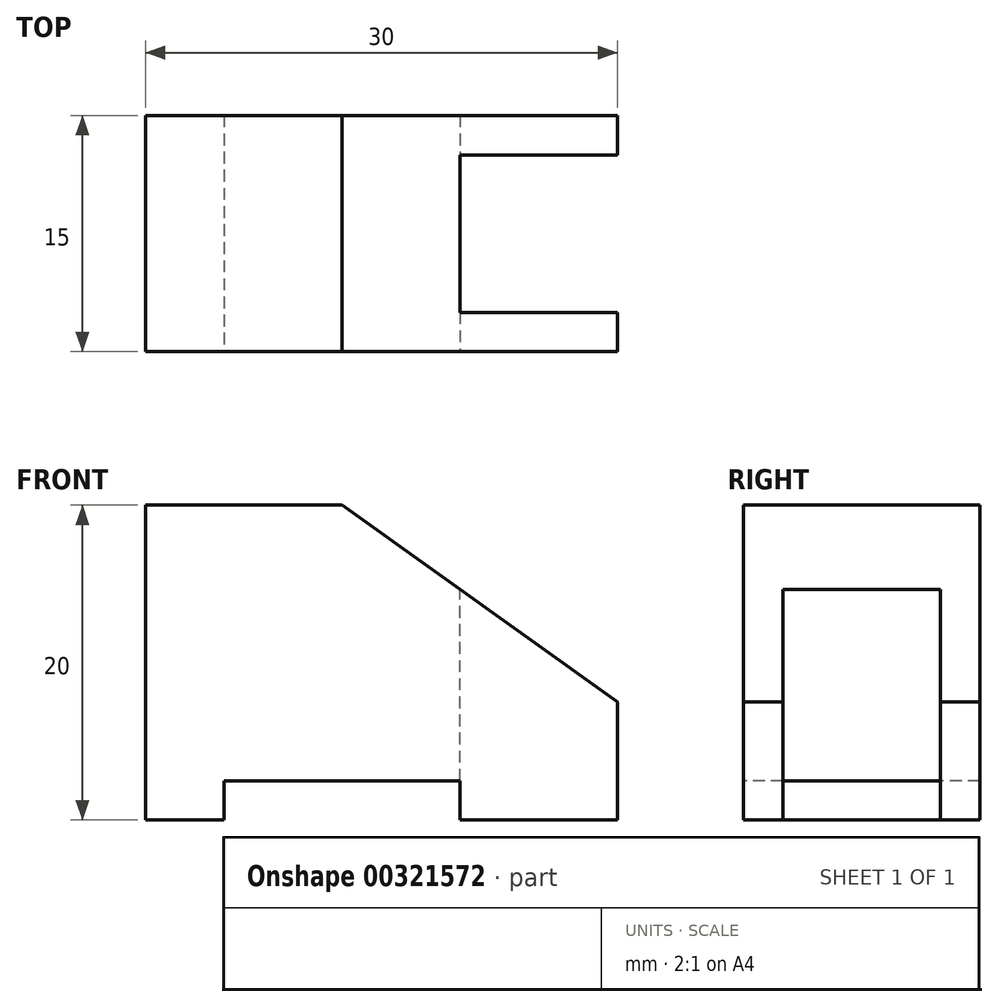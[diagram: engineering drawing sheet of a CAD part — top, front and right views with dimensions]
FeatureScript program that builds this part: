
annotation { "Feature Type Name" : "Feature", "Feature Type Description" : "" }
export const myFeature = defineFeature(function(context is Context, id is Id, definition is map)
    precondition{}
    {
        {
            var Q0;
            Q0=qCreatedBy(makeId("Front.planeOp"),FACE);
            var sketch = newSketch(context, id + "F0", { "sketchPlane" : qUnion([Q0])});
            skLineSegment(sketch, "E0.bottom", {"start": v(0, 0) * mm, "end": v(30, 0) * mm});
            skLineSegment(sketch, "E0.top", {"start": v(0, 20) * mm, "end": v(30, 20) * mm});
            skLineSegment(sketch, "E0.left", {"start": v(0, 0) * mm, "end": v(0, 20) * mm});
            skLineSegment(sketch, "E0.right", {"start": v(30, 0) * mm, "end": v(30, 20) * mm});
            skSolve(sketch);
        }
        {
            var Q0;
            Q0 = qSketchRegion(id + "F0", true);
            extrude(context, id + "F1", {"entities" : qUnion([Q0]), "depth" : 15 * mm});
        }
        {
            var Q0;
            Q0=makeQuery(id+"F1.opExtrude","CAP_FACE",FACE,{"disambiguationData":[OSD([sQuery(id+"F0.wireOp",EDGE,"E0.bottom"),sQuery(id+"F0.wireOp",EDGE,"E0.top"),sQuery(id+"F0.wireOp",EDGE,"E0.left"),sQuery(id+"F0.wireOp",EDGE,"E0.right")])],"isStart":false});
            var sketch = newSketch(context, id + "F2", { "sketchPlane" : qUnion([Q0])});
            skLineSegment(sketch, "E1.bottom", {"start": v(5, 0) * mm, "end": v(20, 0) * mm});
            skLineSegment(sketch, "E1.top", {"start": v(5, 2.5) * mm, "end": v(20, 2.5) * mm});
            skLineSegment(sketch, "E1.left", {"start": v(5, 0) * mm, "end": v(5, 2.5) * mm});
            skLineSegment(sketch, "E1.right", {"start": v(20, 0) * mm, "end": v(20, 2.5) * mm});
            skLineSegment(sketch, "E2", {"start": v(12.5, 20) * mm, "end": v(30, 7.5) * mm});
            skLineSegment(sketch, "E3", {"start": v(30, 7.5) * mm, "end": v(30, 20) * mm});
            skLineSegment(sketch, "E4", {"start": v(30, 20) * mm, "end": v(12.5, 20) * mm});
            skSolve(sketch);
        }
        {
            var Q0;
            Q0 = qSketchRegion(id + "F2", true);
            extrude(context, id + "F3", {"entities" : qUnion([Q0]), "operationType" : NewBodyOperationType.REMOVE, "endBound" : BoundingType.THROUGH_ALL, "oppositeDirection" : true, "depth" : 25 * mm});
        }
        {
            var Q0;
            Q0=makeQuery(id+"F1.opExtrude","SWEPT_FACE",FACE,{"disambiguationData":[OSD([sQuery(id+"F0.wireOp",EDGE,"E0.right")])]});
            var sketch = newSketch(context, id + "F4", { "sketchPlane" : qUnion([Q0])});
            skLineSegment(sketch, "E5.bottom", {"start": v(-12.5, 0) * mm, "end": v(-2.5, 0) * mm});
            skLineSegment(sketch, "E5.top", {"start": v(-12.5, 20) * mm, "end": v(-2.5, 20) * mm});
            skLineSegment(sketch, "E5.left", {"start": v(-12.5, 0) * mm, "end": v(-12.5, 20) * mm});
            skLineSegment(sketch, "E5.right", {"start": v(-2.5, 0) * mm, "end": v(-2.5, 20) * mm});
            skSolve(sketch);
        }
        {
            var Q0;
            Q0 = qSketchRegion(id + "F4", true);
            extrude(context, id + "F5", {"entities" : qUnion([Q0]), "operationType" : NewBodyOperationType.REMOVE, "oppositeDirection" : true, "depth" : 10 * mm});
        }
    });
